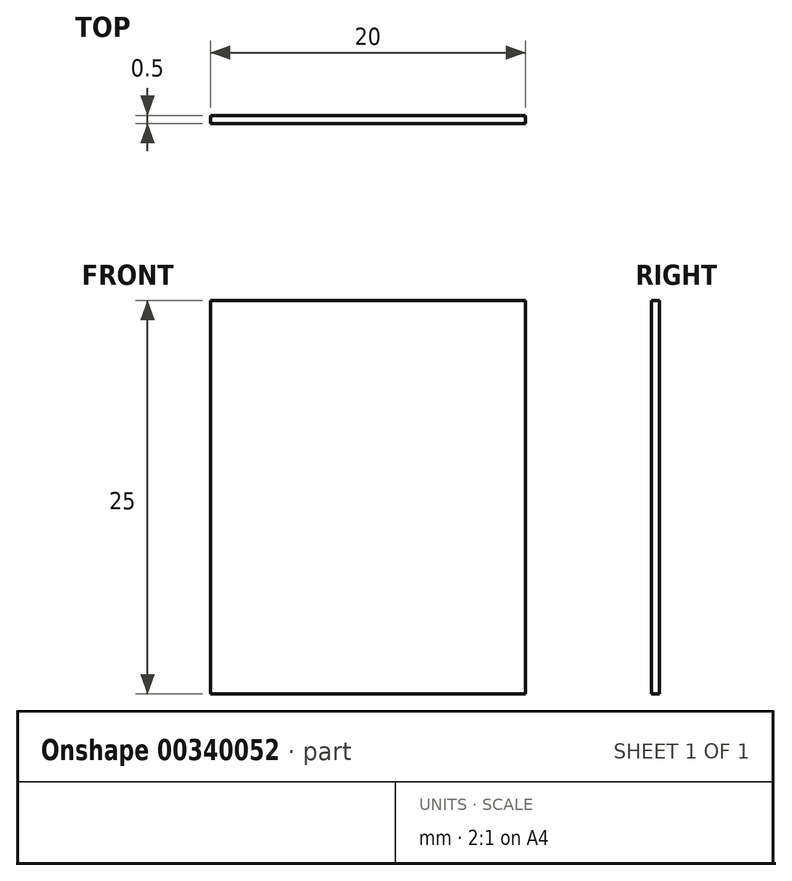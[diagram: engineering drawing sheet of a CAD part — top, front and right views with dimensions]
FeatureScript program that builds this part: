
annotation { "Feature Type Name" : "Feature", "Feature Type Description" : "" }
export const myFeature = defineFeature(function(context is Context, id is Id, definition is map)
    precondition{}
    {
        {
            var Q0;
            Q0=qCreatedBy(makeId("Top.planeOp"),FACE);
            var sketch = newSketch(context, id + "F0", { "sketchPlane" : qUnion([Q0])});
            skLineSegment(sketch, "E0.bottom", {"start": v(0, 0) * mm, "end": v(20, 0) * mm});
            skLineSegment(sketch, "E0.top", {"start": v(0, 0.5) * mm, "end": v(20, 0.5) * mm});
            skLineSegment(sketch, "E0.left", {"start": v(0, 0) * mm, "end": v(0, 0.5) * mm});
            skLineSegment(sketch, "E0.right", {"start": v(20, 0) * mm, "end": v(20, 0.5) * mm});
            skSolve(sketch);
        }
        {
            var Q0;
            Q0 = qSketchRegion(id + "F0", true);
            extrude(context, id + "F1", {"entities" : qUnion([Q0]), "depth" : 25 * mm});
        }
    });
